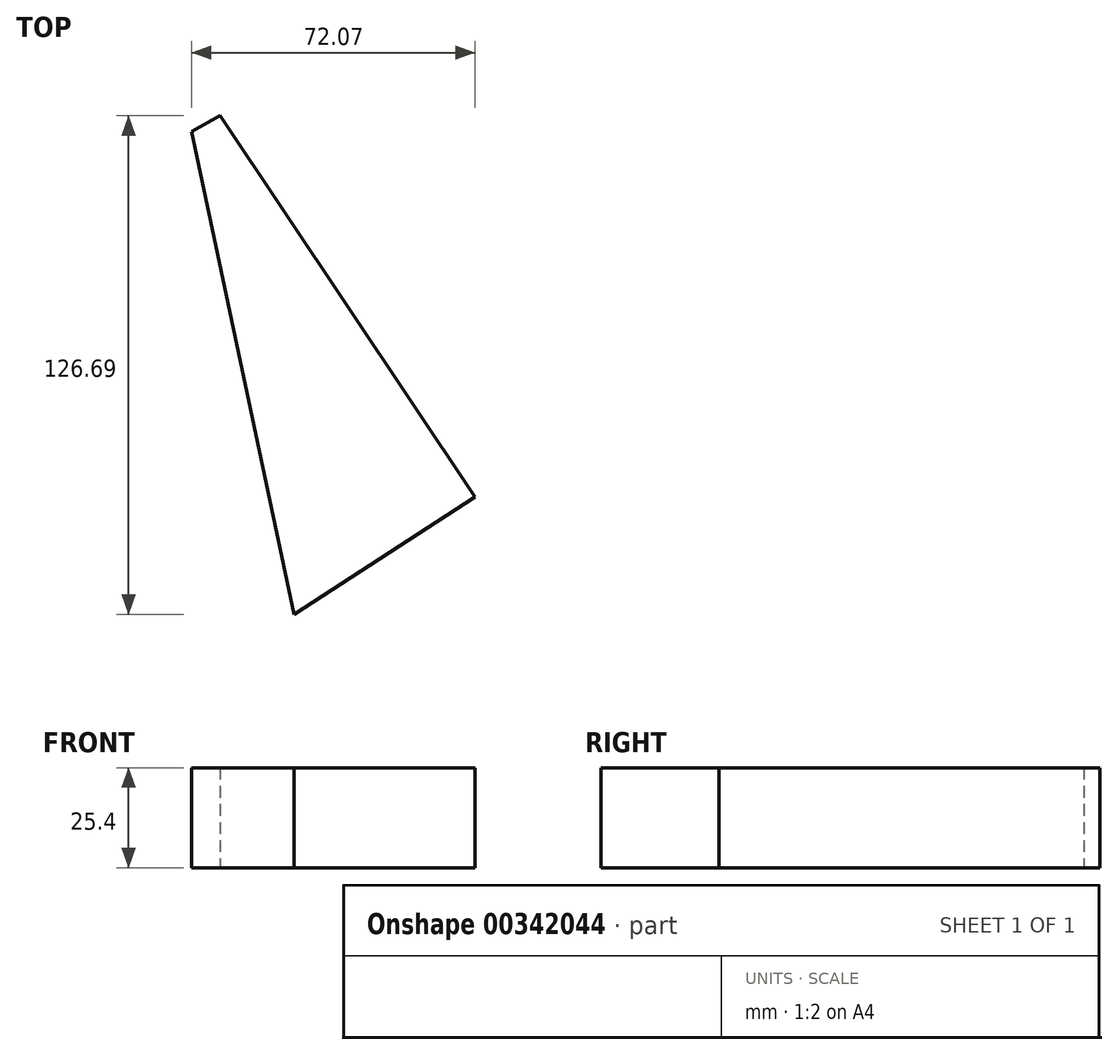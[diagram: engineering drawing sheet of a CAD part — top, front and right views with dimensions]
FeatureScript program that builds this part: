
annotation { "Feature Type Name" : "Feature", "Feature Type Description" : "" }
export const myFeature = defineFeature(function(context is Context, id is Id, definition is map)
    precondition{}
    {
        {
            var Q0;
            Q0=qCreatedBy(makeId("Top.planeOp"),FACE);
            var sketch = newSketch(context, id + "F0", { "sketchPlane" : qUnion([Q0])});
            skLineSegment(sketch, "E0", {"start": v(0, 0) * mm, "end": v(-46, -29.87) * mm});
            skLineSegment(sketch, "E1", {"start": v(-46, -29.87) * mm, "end": v(-72.07, 92.75) * mm});
            skLineSegment(sketch, "E2", {"start": v(-72.07, 92.75) * mm, "end": v(-64.78, 96.82) * mm});
            skLineSegment(sketch, "E3", {"start": v(-64.78, 96.82) * mm, "end": v(0, 0) * mm});
            skLineSegment(sketch, "E4", {"start": v(31.38, -24.66) * mm, "end": v(3.68, -119.8) * mm});
            skSolve(sketch);
        }
        {
            var Q0;
            Q0 = qSketchRegion(id + "F0", true);
            var sketch = newSketch(context, id + "F1", { "sketchPlane" : qUnion([Q0])});
            skSolve(sketch);
        }
        {
            var Q0;
            Q0=makeQuery(id+"F1.imprint","IMPRINT",FACE,{"disambiguationData":[TD([[makeQuery(id+"F1.imprint","IMPRINT",EDGE,{"derivedFrom":makeQuery(id+"F0.imprint","IMPRINT",EDGE,{"derivedFrom":sQuery(id+"F0.wireOp",EDGE,"E0")})}),-1.0]])]});
            extrude(context, id + "F2", {"entities" : qUnion([Q0]), "depth" : 25.4 * mm});
        }
    });
